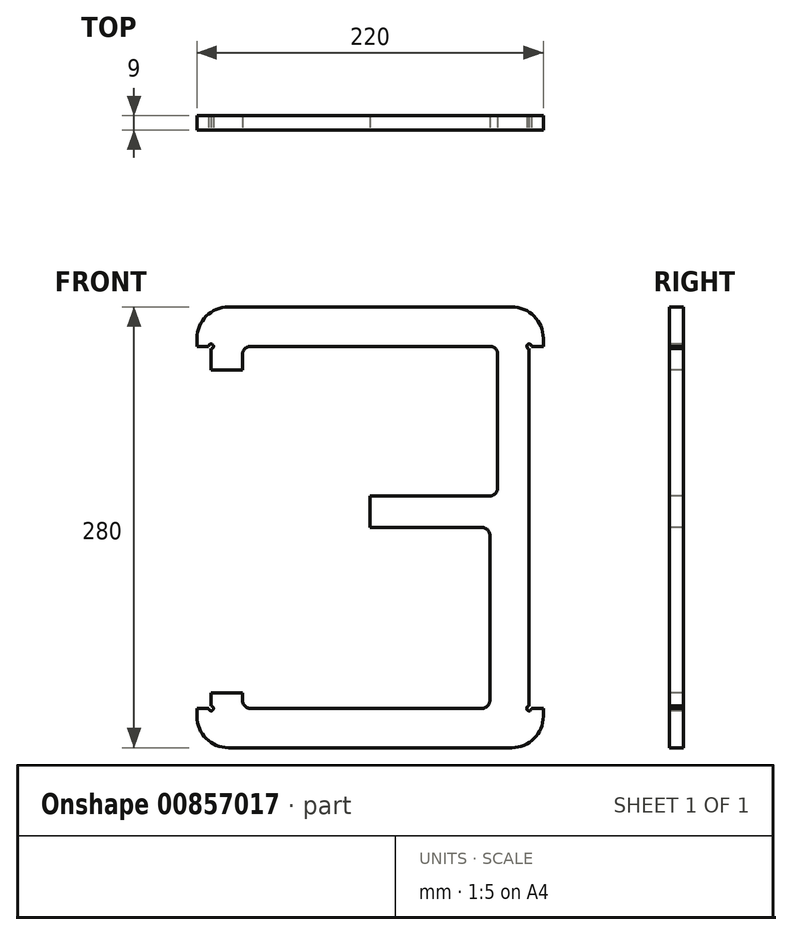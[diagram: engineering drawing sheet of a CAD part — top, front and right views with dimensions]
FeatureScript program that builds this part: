
annotation { "Feature Type Name" : "Feature", "Feature Type Description" : "" }
export const myFeature = defineFeature(function(context is Context, id is Id, definition is map)
    precondition{}
    {
        {
            var Q0;
            Q0=qCreatedBy(makeId("Front.planeOp"),FACE);
            var sketch = newSketch(context, id + "F0", { "sketchPlane" : qUnion([Q0])});
            skLineSegment(sketch, "E0.bottom", {"start": v(-99.41, 134.79) * mm, "end": v(80.59, 134.79) * mm});
            skLineSegment(sketch, "E0.top", {"start": v(-99.41, -145.21) * mm, "end": v(80.59, -145.21) * mm});
            skLineSegment(sketch, "E0.left", {"start": v(-119.41, 114.79) * mm, "end": v(-119.41, 109.79) * mm});
            skLineSegment(sketch, "E0.right", {"start": v(100.59, 114.79) * mm, "end": v(100.59, 109.79) * mm});
            skPoint(sketch, "E0.middle", {"position": v(-9.41, -5.21) * mm});
            skLineSegment(sketch, "E1.bottom", {"start": v(-9.41, 14.79) * mm, "end": v(66.59, 14.79) * mm});
            skLineSegment(sketch, "E2", {"start": v(-119.41, 109.79) * mm, "end": v(-110.41, 109.79) * mm});
            skLineSegment(sketch, "E3", {"start": v(-119.41, -120.21) * mm, "end": v(-110.41, -120.21) * mm});
            skLineSegment(sketch, "E4.0", {"start": v(-110.41, 109.79) * mm, "end": v(-110.41, 94.79) * mm});
            skLineSegment(sketch, "E5.trimOffspring", {"start": v(-119.41, -120.21) * mm, "end": v(-119.41, -125.21) * mm});
            skLineSegment(sketch, "E6.0", {"start": v(-90.41, 104.79) * mm, "end": v(-90.41, 94.79) * mm});
            skLineSegment(sketch, "E7.0", {"start": v(71.59, 104.79) * mm, "end": v(71.59, 84.29) * mm});
            skLineSegment(sketch, "E8.trimOffspring", {"start": v(-85.41, 109.79) * mm, "end": v(66.59, 109.79) * mm});
            skLineSegment(sketch, "E9.trimOffspring", {"start": v(-85.41, -120.21) * mm, "end": v(61.59, -120.21) * mm});
            skLineSegment(sketch, "E10.trimOffspring", {"start": v(-9.41, -5.21) * mm, "end": v(61.59, -5.21) * mm});
            skPoint(sketch, "E11.visualSharp", {"position": v(-119.41, 134.79) * mm});
            skArc(sketch, "E11.filletArc", {"start": v(-99.41, 134.79) * mm, "mid": v(-113.55, 128.93) * mm, "end": v(-119.41, 114.79) * mm});
            skPoint(sketch, "E12.visualSharp", {"position": v(100.59, 134.79) * mm});
            skArc(sketch, "E12.filletArc", {"start": v(100.59, 114.79) * mm, "mid": v(94.73, 128.93) * mm, "end": v(80.59, 134.79) * mm});
            skPoint(sketch, "E13.visualSharp", {"position": v(100.59, -145.21) * mm});
            skArc(sketch, "E13.filletArc", {"start": v(80.59, -145.21) * mm, "mid": v(94.73, -139.35) * mm, "end": v(100.59, -125.21) * mm});
            skPoint(sketch, "E14.visualSharp", {"position": v(-119.41, -145.21) * mm});
            skArc(sketch, "E14.filletArc", {"start": v(-119.41, -125.21) * mm, "mid": v(-113.55, -139.35) * mm, "end": v(-99.41, -145.21) * mm});
            skLineSegment(sketch, "E15.trimOffspring", {"start": v(100.59, -120.21) * mm, "end": v(100.59, -125.21) * mm});
            skLineSegment(sketch, "E16.trimOffspring", {"start": v(91.59, -120.21) * mm, "end": v(100.59, -120.21) * mm});
            skLineSegment(sketch, "E17.trimOffspring", {"start": v(91.59, 109.79) * mm, "end": v(91.59, 84.29) * mm});
            skLineSegment(sketch, "E18.trimOffspring", {"start": v(91.59, 109.79) * mm, "end": v(100.59, 109.79) * mm});
            skPoint(sketch, "E19.visualSharp", {"position": v(71.59, 14.79) * mm});
            skArc(sketch, "E19.filletArc", {"start": v(66.59, 14.79) * mm, "mid": v(70.13, 16.25) * mm, "end": v(71.59, 19.79) * mm});
            skPoint(sketch, "E20.visualSharp", {"position": v(-90.41, 14.79) * mm});
            skPoint(sketch, "E21.visualSharp", {"position": v(-90.41, -5.21) * mm});
            skPoint(sketch, "E22.visualSharp", {"position": v(-90.41, -120.21) * mm});
            skArc(sketch, "E22.filletArc", {"start": v(-90.41, -115.21) * mm, "mid": v(-88.95, -118.75) * mm, "end": v(-85.41, -120.21) * mm});
            skPoint(sketch, "E23.visualSharp", {"position": v(-90.41, 109.79) * mm});
            skArc(sketch, "E23.filletArc", {"start": v(-85.41, 109.79) * mm, "mid": v(-88.95, 108.32) * mm, "end": v(-90.41, 104.79) * mm});
            skPoint(sketch, "E24.visualSharp", {"position": v(71.59, 109.79) * mm});
            skArc(sketch, "E24.filletArc", {"start": v(71.59, 104.79) * mm, "mid": v(70.13, 108.32) * mm, "end": v(66.59, 109.79) * mm});
            skCircle(sketch, "E25", {"center": v(-110.41, 109.79) * mm, "radius": 1.5 * mm});
            skCircle(sketch, "E26", {"center": v(91.59, 109.79) * mm, "radius": 1.5 * mm});
            skCircle(sketch, "E27", {"center": v(-110.41, -120.21) * mm, "radius": 1.5 * mm});
            skCircle(sketch, "E28", {"center": v(91.59, -120.21) * mm, "radius": 1.5 * mm});
            skLineSegment(sketch, "E29.bottom", {"start": v(-110.41, 94.79) * mm, "end": v(-90.41, 94.79) * mm});
            skLineSegment(sketch, "E29.top", {"start": v(-110.41, -110.21) * mm, "end": v(-90.41, -110.21) * mm});
            skLineSegment(sketch, "E29.right", {"start": v(91.59, 51.29) * mm, "end": v(91.59, -15.21) * mm});
            skLineSegment(sketch, "E30.trimOffspring", {"start": v(-90.41, -110.21) * mm, "end": v(-90.41, -115.21) * mm});
            skLineSegment(sketch, "E31.trimOffspring", {"start": v(-110.41, -110.21) * mm, "end": v(-110.41, -120.21) * mm});
            skLineSegment(sketch, "E32.left", {"start": v(-85.41, -5.21) * mm, "end": v(-85.41, -5.38) * mm});
            skPoint(sketch, "E33", {"position": v(91.59, -60.21) * mm});
            skLineSegment(sketch, "E34", {"start": v(91.59, -60.21) * mm, "end": v(76.59, -60.21) * mm});
            skLineSegment(sketch, "E35", {"start": v(91.59, -15.21) * mm, "end": v(76.59, -15.21) * mm});
            skLineSegment(sketch, "E36", {"start": v(76.59, -60.21) * mm, "end": v(76.59, -15.21) * mm});
            skLineSegment(sketch, "E37.trimOffspring", {"start": v(91.59, -60.21) * mm, "end": v(91.59, -110.21) * mm});
            skLineSegment(sketch, "E38.trimOffspring", {"start": v(91.59, -60.21) * mm, "end": v(91.59, -120.21) * mm});
            skLineSegment(sketch, "E39", {"start": v(66.59, -10.21) * mm, "end": v(66.59, -35.87) * mm});
            skLineSegment(sketch, "E40", {"start": v(66.59, -35.87) * mm, "end": v(66.59, -115.21) * mm});
            skPoint(sketch, "E41.visualSharp", {"position": v(66.59, -5.21) * mm});
            skArc(sketch, "E41.filletArc", {"start": v(66.59, -10.21) * mm, "mid": v(65.13, -6.68) * mm, "end": v(61.59, -5.21) * mm});
            skPoint(sketch, "E42.visualSharp", {"position": v(66.59, -120.21) * mm});
            skArc(sketch, "E42.filletArc", {"start": v(61.59, -120.21) * mm, "mid": v(65.13, -118.75) * mm, "end": v(66.59, -115.21) * mm});
            skPoint(sketch, "E43", {"position": v(56.25, 84.29) * mm});
            skPoint(sketch, "E44", {"position": v(61.33, 51.29) * mm});
            skLineSegment(sketch, "E45", {"start": v(71.59, 84.29) * mm, "end": v(91.59, 84.29) * mm});
            skLineSegment(sketch, "E46", {"start": v(71.59, 51.29) * mm, "end": v(91.59, 51.29) * mm});
            skLineSegment(sketch, "E47.trimOffspring", {"start": v(71.59, 51.29) * mm, "end": v(71.59, 19.79) * mm});
            skPoint(sketch, "E48.orphan", {"position": v(91.59, 79.79) * mm});
            skLineSegment(sketch, "E49", {"start": v(-9.41, -5.21) * mm, "end": v(-9.41, 14.79) * mm});
            skPoint(sketch, "E32.bottom.start.orphan", {"position": v(-85.41, 14.79) * mm});
            skLineSegment(sketch, "E50", {"start": v(71.59, 84.29) * mm, "end": v(71.59, 51.29) * mm});
            skLineSegment(sketch, "E51", {"start": v(91.59, 84.29) * mm, "end": v(91.59, 51.29) * mm});
            skLineSegment(sketch, "E52", {"start": v(91.59, -15.21) * mm, "end": v(91.59, -60.21) * mm});
            skSolve(sketch);
        }
        {
            var Q0;
            Q0=makeQuery(id+"F0.imprint","IMPRINT",FACE,{"disambiguationData":[TD([[makeQuery(id+"F0.imprint","IMPRINT",EDGE,{"derivedFrom":sQuery(id+"F0.wireOp",EDGE,"E0.bottom")}),-1.0]])]});
            var Q1;
            Q1=makeQuery(id+"F0.imprint","IMPRINT",FACE,{"disambiguationData":[TD([[makeQuery(id+"F0.imprint","IMPRINT",EDGE,{"derivedFrom":sQuery(id+"F0.wireOp",EDGE,"E0.top")}),1.0]])]});
            var Q2;
            Q2=makeQuery(id+"F0.imprint","IMPRINT",FACE,{"disambiguationData":[TD([[makeQuery(id+"F0.imprint","IMPRINT",EDGE,{"derivedFrom":sQuery(id+"F0.wireOp",EDGE,"E45")}),-1.0]])]});
            var Q3;
            Q3=makeQuery(id+"F0.imprint","IMPRINT",FACE,{"disambiguationData":[TD([[makeQuery(id+"F0.imprint","IMPRINT",EDGE,{"derivedFrom":sQuery(id+"F0.wireOp",EDGE,"E34")}),-1.0]])]});
            extrude(context, id + "F1", {"entities" : qUnion([Q0, Q1, Q2, Q3]), "oppositeDirection" : true, "depth" : 9 * mm, "offsetDistance" : 25 * mm});
        }
    });
